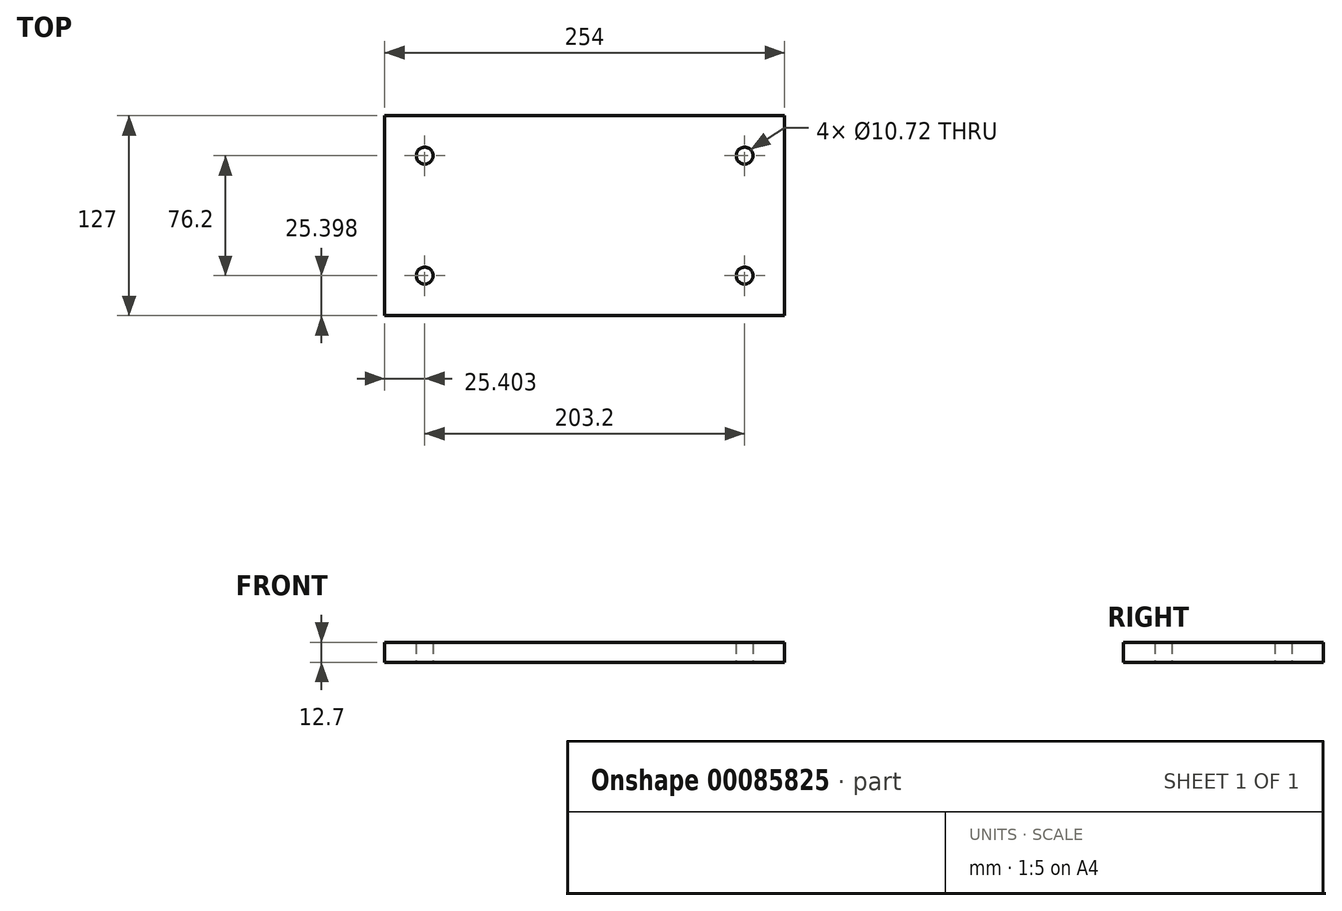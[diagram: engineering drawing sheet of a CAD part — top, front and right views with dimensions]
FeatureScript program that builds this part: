
annotation { "Feature Type Name" : "Feature", "Feature Type Description" : "" }
export const myFeature = defineFeature(function(context is Context, id is Id, definition is map)
    precondition{}
    {
        {
            var Q0;
            Q0=qCreatedBy(makeId("Top.planeOp"),FACE);
            var sketch = newSketch(context, id + "F0", { "sketchPlane" : qUnion([Q0])});
            skLineSegment(sketch, "E0.bottom", {"start": v(116.38, -66.85) * mm, "end": v(-137.62, -66.85) * mm});
            skLineSegment(sketch, "E0.top", {"start": v(116.38, 60.15) * mm, "end": v(-137.62, 60.15) * mm});
            skLineSegment(sketch, "E0.left", {"start": v(116.38, -66.85) * mm, "end": v(116.38, 60.15) * mm});
            skLineSegment(sketch, "E0.right", {"start": v(-137.62, -66.85) * mm, "end": v(-137.62, 60.15) * mm});
            skSolve(sketch);
        }
        {
            var Q0;
            Q0=makeQuery(id+"F0.imprint","IMPRINT",FACE,{"disambiguationData":[TD([[makeQuery(id+"F0.imprint","IMPRINT",EDGE,{"derivedFrom":sQuery(id+"F0.wireOp",EDGE,"E0.bottom")}),-1.0]])]});
            extrude(context, id + "F1", {"entities" : qUnion([Q0]), "depth" : 12.7 * mm, "offsetDistance" : 25.4 * mm});
        }
        {
            var Q0;
            Q0=makeQuery(id+"F1.opExtrude","CAP_FACE",FACE,{"disambiguationData":[OSD([sQuery(id+"F0.wireOp",EDGE,"E0.bottom"),sQuery(id+"F0.wireOp",EDGE,"E0.top"),sQuery(id+"F0.wireOp",EDGE,"E0.left"),sQuery(id+"F0.wireOp",EDGE,"E0.right")])],"isStart":false});
            var sketch = newSketch(context, id + "F2", { "sketchPlane" : qUnion([Q0])});
            skPoint(sketch, "E1", {"position": v(-112.22, 34.75) * mm});
            skLineSegment(sketch, "E2", {"start": v(-10.62, 60.15) * mm, "end": v(-10.62, -66.85) * mm});
            skLineSegment(sketch, "E3", {"start": v(-137.62, -3.35) * mm, "end": v(116.38, -3.35) * mm});
            skPoint(sketch, "E4.MirrorP", {"position": v(90.98, 34.75) * mm});
            skPoint(sketch, "E5.MirrorP", {"position": v(-112.22, -41.45) * mm});
            skPoint(sketch, "E6.MirrorP", {"position": v(90.98, -41.45) * mm});
            skSolve(sketch);
        }
        {
            var Q0;
            Q0=sQuery(id+"F2.wireOp",VERTEX,"E1");
            var Q1;
            Q1=sQuery(id+"F2.wireOp",VERTEX,"E5.MirrorP");
            var Q2;
            Q2=sQuery(id+"F2.wireOp",VERTEX,"E4.MirrorP");
            var Q3;
            Q3=sQuery(id+"F2.wireOp",VERTEX,"E6.MirrorP");
            var Q4;
            Q4=makeQuery(id+"F1.opExtrude","SWEPT_BODY",BODY,{"disambiguationData":[OSD([sQuery(id+"F0.wireOp",EDGE,"E0.bottom"),sQuery(id+"F0.wireOp",EDGE,"E0.top"),sQuery(id+"F0.wireOp",EDGE,"E0.left"),sQuery(id+"F0.wireOp",EDGE,"E0.right")])]});
            hole(context, id + "F3", {"style" : HoleStyle.SIMPLE, "endStyle" : HoleEndStyle.THROUGH, "standardTappedOrClearance" : lookupTablePath({ "standard" : "ANSI", "engagement" : "75%", "pitch" : "13 tpi", "size" : "1/2", "type" : "Tapped" }), "standardBlindInLast" : lookupTablePath({ "standard" : "ANSI", "engagement" : "75%", "pitch" : "13 tpi", "size" : "1/2", "type" : "Tapped" }), "holeDiameter" : 10.72 * mm, "majorDiameter" : 12.7 * mm, "showTappedDepth" : true, "isTappedThrough" : true, "tappedDepth" : 12.7 * mm, "tapClearance" : 3, "locations" : qUnion([Q0, Q1, Q2, Q3]), "scope" : qUnion([Q4])});
        }
    });
